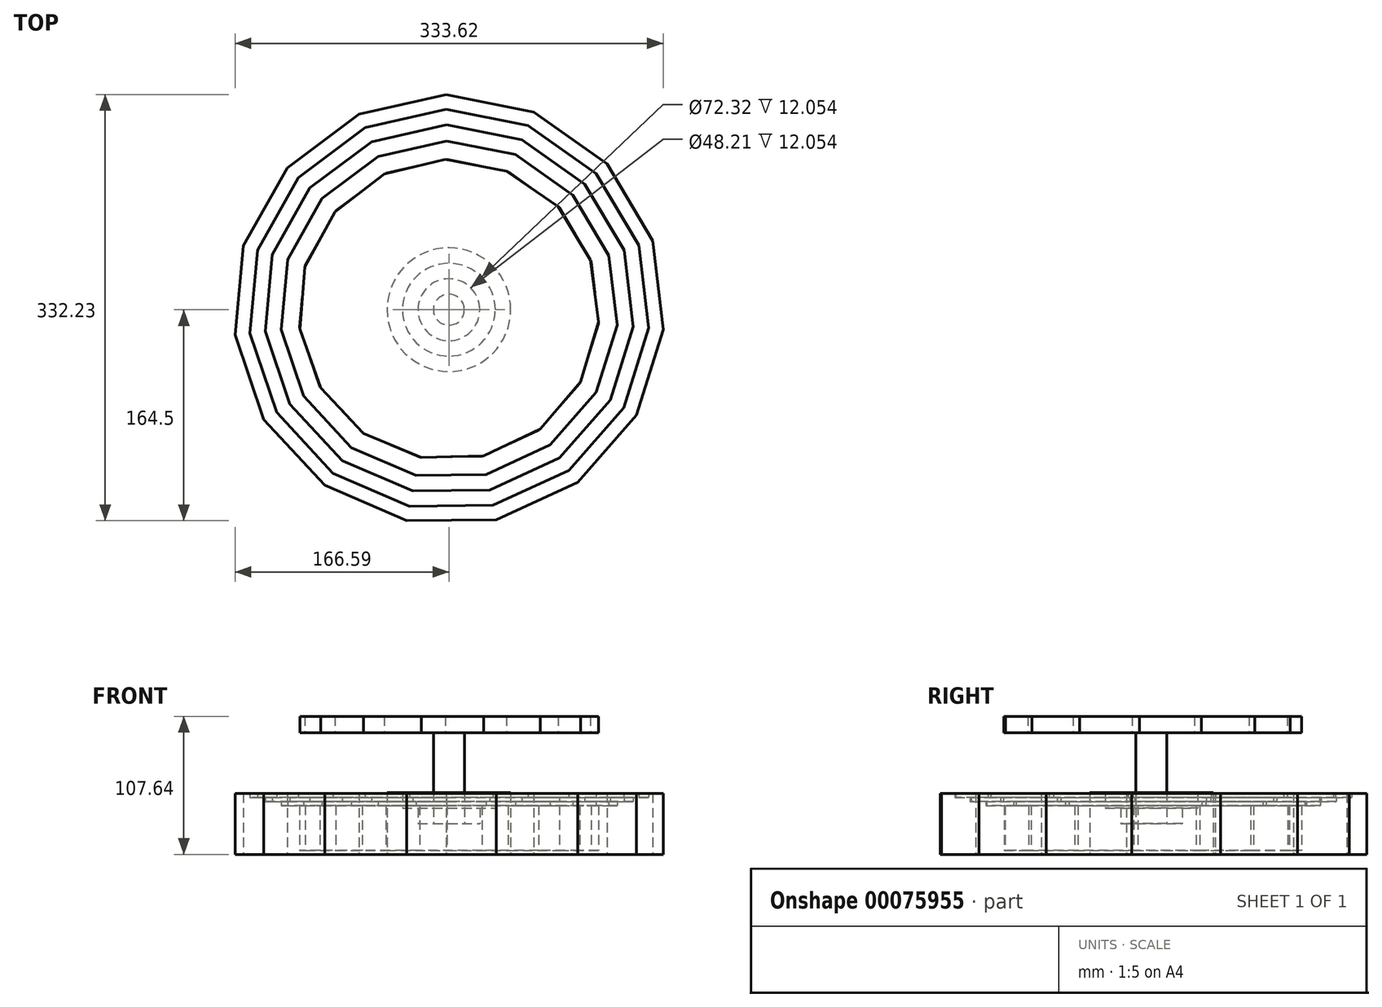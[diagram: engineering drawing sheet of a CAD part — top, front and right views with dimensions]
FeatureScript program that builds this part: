
annotation { "Feature Type Name" : "Feature", "Feature Type Description" : "" }
export const myFeature = defineFeature(function(context is Context, id is Id, definition is map)
    precondition{}
    {
        {
            var Q0;
            Q0=qCreatedBy(makeId("Top.planeOp"),FACE);
            var sketch = newSketch(context, id + "F0", { "sketchPlane" : qUnion([Q0])});
            skCircle(sketch, "E0.cCircle", {"center": v(0, 0) * mm, "radius": 164.07 * mm, "construction": true});
            skLineSegment(sketch, "E0.0", {"start": v(-160.17, 49.81) * mm, "end": v(-126.07, 110.65) * mm});
            skLineSegment(sketch, "E0.1", {"start": v(-126.07, 110.65) * mm, "end": v(-70.16, 152.36) * mm});
            skLineSegment(sketch, "E0.2", {"start": v(-70.16, 152.36) * mm, "end": v(-2.12, 167.73) * mm});
            skLineSegment(sketch, "E0.3", {"start": v(-2.12, 167.73) * mm, "end": v(66.28, 154.09) * mm});
            skLineSegment(sketch, "E0.4", {"start": v(66.28, 154.09) * mm, "end": v(123.22, 113.8) * mm});
            skLineSegment(sketch, "E0.5", {"start": v(123.22, 113.8) * mm, "end": v(158.86, 53.85) * mm});
            skLineSegment(sketch, "E0.6", {"start": v(158.86, 53.85) * mm, "end": v(167.03, -15.42) * mm});
            skLineSegment(sketch, "E0.7", {"start": v(167.03, -15.42) * mm, "end": v(146.32, -82.02) * mm});
            skLineSegment(sketch, "E0.8", {"start": v(146.32, -82.02) * mm, "end": v(100.3, -134.45) * mm});
            skLineSegment(sketch, "E0.9", {"start": v(100.3, -134.45) * mm, "end": v(36.95, -163.62) * mm});
            skLineSegment(sketch, "E0.10", {"start": v(36.95, -163.62) * mm, "end": v(-32.8, -164.5) * mm});
            skLineSegment(sketch, "E0.11", {"start": v(-32.8, -164.5) * mm, "end": v(-96.87, -136.94) * mm});
            skLineSegment(sketch, "E0.12", {"start": v(-96.87, -136.94) * mm, "end": v(-144.2, -85.7) * mm});
            skLineSegment(sketch, "E0.13", {"start": v(-144.2, -85.7) * mm, "end": v(-166.59, -19.64) * mm});
            skLineSegment(sketch, "E0.14", {"start": v(-166.59, -19.64) * mm, "end": v(-160.17, 49.81) * mm});
            skPoint(sketch, "E0.0.midPoint", {"position": v(-143.12, 80.23) * mm});
            skCircle(sketch, "E1.cCircle", {"center": v(0, 0) * mm, "radius": 152.82 * mm, "construction": true});
            skLineSegment(sketch, "E1.0", {"start": v(-149.18, 46.4) * mm, "end": v(-117.42, 103.06) * mm});
            skLineSegment(sketch, "E1.1", {"start": v(-117.42, 103.06) * mm, "end": v(-65.35, 141.9) * mm});
            skLineSegment(sketch, "E1.2", {"start": v(-65.35, 141.9) * mm, "end": v(-1.98, 156.22) * mm});
            skLineSegment(sketch, "E1.3", {"start": v(-1.98, 156.22) * mm, "end": v(61.73, 143.52) * mm});
            skLineSegment(sketch, "E1.4", {"start": v(61.73, 143.52) * mm, "end": v(114.77, 106) * mm});
            skLineSegment(sketch, "E1.5", {"start": v(114.77, 106) * mm, "end": v(147.96, 50.15) * mm});
            skLineSegment(sketch, "E1.6", {"start": v(147.96, 50.15) * mm, "end": v(155.57, -14.36) * mm});
            skLineSegment(sketch, "E1.7", {"start": v(155.57, -14.36) * mm, "end": v(136.28, -76.4) * mm});
            skLineSegment(sketch, "E1.8", {"start": v(136.28, -76.4) * mm, "end": v(93.42, -125.22) * mm});
            skLineSegment(sketch, "E1.9", {"start": v(93.42, -125.22) * mm, "end": v(34.41, -152.4) * mm});
            skLineSegment(sketch, "E1.10", {"start": v(34.41, -152.4) * mm, "end": v(-30.55, -153.21) * mm});
            skLineSegment(sketch, "E1.11", {"start": v(-30.55, -153.21) * mm, "end": v(-90.22, -127.54) * mm});
            skLineSegment(sketch, "E1.12", {"start": v(-90.22, -127.54) * mm, "end": v(-134.3, -79.82) * mm});
            skLineSegment(sketch, "E1.13", {"start": v(-134.3, -79.82) * mm, "end": v(-155.15, -18.3) * mm});
            skLineSegment(sketch, "E1.14", {"start": v(-155.15, -18.3) * mm, "end": v(-149.18, 46.4) * mm});
            skPoint(sketch, "E1.0.midPoint", {"position": v(-133.3, 74.73) * mm});
            skCircle(sketch, "E2.cCircle", {"center": v(0, 0) * mm, "radius": 140.97 * mm, "construction": true});
            skLineSegment(sketch, "E2.0", {"start": v(-137.62, 42.8) * mm, "end": v(-108.32, 95.07) * mm});
            skLineSegment(sketch, "E2.1", {"start": v(-108.32, 95.07) * mm, "end": v(-60.28, 130.91) * mm});
            skLineSegment(sketch, "E2.2", {"start": v(-60.28, 130.91) * mm, "end": v(-1.82, 144.11) * mm});
            skLineSegment(sketch, "E2.3", {"start": v(-1.82, 144.11) * mm, "end": v(56.95, 132.4) * mm});
            skLineSegment(sketch, "E2.4", {"start": v(56.95, 132.4) * mm, "end": v(105.88, 97.79) * mm});
            skLineSegment(sketch, "E2.5", {"start": v(105.88, 97.79) * mm, "end": v(136.5, 46.27) * mm});
            skLineSegment(sketch, "E2.6", {"start": v(136.5, 46.27) * mm, "end": v(143.51, -13.25) * mm});
            skLineSegment(sketch, "E2.7", {"start": v(143.51, -13.25) * mm, "end": v(125.72, -70.48) * mm});
            skLineSegment(sketch, "E2.8", {"start": v(125.72, -70.48) * mm, "end": v(86.18, -115.52) * mm});
            skLineSegment(sketch, "E2.9", {"start": v(86.18, -115.52) * mm, "end": v(31.75, -140.58) * mm});
            skLineSegment(sketch, "E2.10", {"start": v(31.75, -140.58) * mm, "end": v(-28.18, -141.34) * mm});
            skLineSegment(sketch, "E2.11", {"start": v(-28.18, -141.34) * mm, "end": v(-83.23, -117.66) * mm});
            skLineSegment(sketch, "E2.12", {"start": v(-83.23, -117.66) * mm, "end": v(-123.9, -73.64) * mm});
            skLineSegment(sketch, "E2.13", {"start": v(-123.9, -73.64) * mm, "end": v(-143.13, -16.88) * mm});
            skLineSegment(sketch, "E2.14", {"start": v(-143.13, -16.88) * mm, "end": v(-137.62, 42.8) * mm});
            skPoint(sketch, "E2.0.midPoint", {"position": v(-122.97, 68.94) * mm});
            skCircle(sketch, "E3.cCircle", {"center": v(0, 0) * mm, "radius": 128.76 * mm, "construction": true});
            skLineSegment(sketch, "E3.0", {"start": v(-125.7, 39.1) * mm, "end": v(-98.94, 86.84) * mm});
            skLineSegment(sketch, "E3.1", {"start": v(-98.94, 86.84) * mm, "end": v(-55.06, 119.57) * mm});
            skLineSegment(sketch, "E3.2", {"start": v(-55.06, 119.57) * mm, "end": v(-1.67, 131.63) * mm});
            skLineSegment(sketch, "E3.3", {"start": v(-1.67, 131.63) * mm, "end": v(52.02, 120.93) * mm});
            skLineSegment(sketch, "E3.4", {"start": v(52.02, 120.93) * mm, "end": v(96.7, 89.32) * mm});
            skLineSegment(sketch, "E3.5", {"start": v(96.7, 89.32) * mm, "end": v(124.67, 42.26) * mm});
            skLineSegment(sketch, "E3.6", {"start": v(124.67, 42.26) * mm, "end": v(131.08, -12.1) * mm});
            skLineSegment(sketch, "E3.7", {"start": v(131.08, -12.1) * mm, "end": v(114.83, -64.37) * mm});
            skLineSegment(sketch, "E3.8", {"start": v(114.83, -64.37) * mm, "end": v(78.72, -105.51) * mm});
            skLineSegment(sketch, "E3.9", {"start": v(78.72, -105.51) * mm, "end": v(29, -128.4) * mm});
            skLineSegment(sketch, "E3.10", {"start": v(29, -128.4) * mm, "end": v(-25.74, -129.1) * mm});
            skLineSegment(sketch, "E3.11", {"start": v(-25.74, -129.1) * mm, "end": v(-76.02, -107.47) * mm});
            skLineSegment(sketch, "E3.12", {"start": v(-76.02, -107.47) * mm, "end": v(-113.16, -67.26) * mm});
            skLineSegment(sketch, "E3.13", {"start": v(-113.16, -67.26) * mm, "end": v(-130.74, -15.42) * mm});
            skLineSegment(sketch, "E3.14", {"start": v(-130.74, -15.42) * mm, "end": v(-125.7, 39.1) * mm});
            skPoint(sketch, "E3.0.midPoint", {"position": v(-112.32, 62.97) * mm});
            skCircle(sketch, "E4.cCircle", {"center": v(0, 0) * mm, "radius": 114.54 * mm, "construction": true});
            skLineSegment(sketch, "E4.0", {"start": v(-111.81, 34.77) * mm, "end": v(-88, 77.24) * mm});
            skLineSegment(sketch, "E4.1", {"start": v(-88, 77.24) * mm, "end": v(-48.98, 106.36) * mm});
            skLineSegment(sketch, "E4.2", {"start": v(-48.98, 106.36) * mm, "end": v(-1.48, 117.08) * mm});
            skLineSegment(sketch, "E4.3", {"start": v(-1.48, 117.08) * mm, "end": v(46.27, 107.57) * mm});
            skLineSegment(sketch, "E4.4", {"start": v(46.27, 107.57) * mm, "end": v(86.02, 79.45) * mm});
            skLineSegment(sketch, "E4.5", {"start": v(86.02, 79.45) * mm, "end": v(110.9, 37.6) * mm});
            skLineSegment(sketch, "E4.6", {"start": v(110.9, 37.6) * mm, "end": v(116.6, -10.76) * mm});
            skLineSegment(sketch, "E4.7", {"start": v(116.6, -10.76) * mm, "end": v(102.14, -57.26) * mm});
            skLineSegment(sketch, "E4.8", {"start": v(102.14, -57.26) * mm, "end": v(70.02, -93.85) * mm});
            skLineSegment(sketch, "E4.9", {"start": v(70.02, -93.85) * mm, "end": v(25.8, -114.22) * mm});
            skLineSegment(sketch, "E4.10", {"start": v(25.8, -114.22) * mm, "end": v(-22.9, -114.83) * mm});
            skLineSegment(sketch, "E4.11", {"start": v(-22.9, -114.83) * mm, "end": v(-67.62, -95.6) * mm});
            skLineSegment(sketch, "E4.12", {"start": v(-67.62, -95.6) * mm, "end": v(-100.66, -59.83) * mm});
            skLineSegment(sketch, "E4.13", {"start": v(-100.66, -59.83) * mm, "end": v(-116.29, -13.71) * mm});
            skLineSegment(sketch, "E4.14", {"start": v(-116.29, -13.71) * mm, "end": v(-111.81, 34.77) * mm});
            skPoint(sketch, "E4.0.midPoint", {"position": v(-99.9, 56) * mm});
            skCircle(sketch, "E5.cCircle", {"center": v(0, 0) * mm, "radius": 101.53 * mm, "construction": true});
            skLineSegment(sketch, "E5.0", {"start": v(-99.12, 30.82) * mm, "end": v(-78, 68.47) * mm});
            skLineSegment(sketch, "E5.1", {"start": v(-78, 68.47) * mm, "end": v(-43.42, 94.28) * mm});
            skLineSegment(sketch, "E5.2", {"start": v(-43.42, 94.28) * mm, "end": v(-1.31, 103.79) * mm});
            skLineSegment(sketch, "E5.3", {"start": v(-1.31, 103.79) * mm, "end": v(41.01, 95.35) * mm});
            skLineSegment(sketch, "E5.4", {"start": v(41.01, 95.35) * mm, "end": v(76.25, 70.43) * mm});
            skLineSegment(sketch, "E5.5", {"start": v(76.25, 70.43) * mm, "end": v(98.3, 33.32) * mm});
            skLineSegment(sketch, "E5.6", {"start": v(98.3, 33.32) * mm, "end": v(103.36, -9.54) * mm});
            skLineSegment(sketch, "E5.7", {"start": v(103.36, -9.54) * mm, "end": v(90.54, -50.76) * mm});
            skLineSegment(sketch, "E5.8", {"start": v(90.54, -50.76) * mm, "end": v(62.07, -83.2) * mm});
            skLineSegment(sketch, "E5.9", {"start": v(62.07, -83.2) * mm, "end": v(22.86, -101.25) * mm});
            skLineSegment(sketch, "E5.10", {"start": v(22.86, -101.25) * mm, "end": v(-20.3, -101.8) * mm});
            skLineSegment(sketch, "E5.11", {"start": v(-20.3, -101.8) * mm, "end": v(-59.94, -84.74) * mm});
            skLineSegment(sketch, "E5.12", {"start": v(-59.94, -84.74) * mm, "end": v(-89.23, -53.03) * mm});
            skLineSegment(sketch, "E5.13", {"start": v(-89.23, -53.03) * mm, "end": v(-103.08, -12.16) * mm});
            skLineSegment(sketch, "E5.14", {"start": v(-103.08, -12.16) * mm, "end": v(-99.12, 30.82) * mm});
            skPoint(sketch, "E5.0.midPoint", {"position": v(-88.56, 49.65) * mm});
            skCircle(sketch, "E6.cCircle", {"center": v(0, 0) * mm, "radius": 89.42 * mm, "construction": true});
            skLineSegment(sketch, "E6.0", {"start": v(-87.3, 27.15) * mm, "end": v(-68.7, 60.3) * mm});
            skLineSegment(sketch, "E6.1", {"start": v(-68.7, 60.3) * mm, "end": v(-38.24, 83.03) * mm});
            skLineSegment(sketch, "E6.2", {"start": v(-38.24, 83.03) * mm, "end": v(-1.16, 91.4) * mm});
            skLineSegment(sketch, "E6.3", {"start": v(-1.16, 91.4) * mm, "end": v(36.12, 83.97) * mm});
            skLineSegment(sketch, "E6.4", {"start": v(36.12, 83.97) * mm, "end": v(67.15, 62.02) * mm});
            skLineSegment(sketch, "E6.5", {"start": v(67.15, 62.02) * mm, "end": v(86.58, 29.35) * mm});
            skLineSegment(sketch, "E6.6", {"start": v(86.58, 29.35) * mm, "end": v(91.03, -8.4) * mm});
            skLineSegment(sketch, "E6.7", {"start": v(91.03, -8.4) * mm, "end": v(79.74, -44.7) * mm});
            skLineSegment(sketch, "E6.8", {"start": v(79.74, -44.7) * mm, "end": v(54.66, -73.27) * mm});
            skLineSegment(sketch, "E6.9", {"start": v(54.66, -73.27) * mm, "end": v(20.14, -89.17) * mm});
            skLineSegment(sketch, "E6.10", {"start": v(20.14, -89.17) * mm, "end": v(-17.87, -89.65) * mm});
            skLineSegment(sketch, "E6.11", {"start": v(-17.87, -89.65) * mm, "end": v(-52.8, -74.63) * mm});
            skLineSegment(sketch, "E6.12", {"start": v(-52.8, -74.63) * mm, "end": v(-78.58, -46.7) * mm});
            skLineSegment(sketch, "E6.13", {"start": v(-78.58, -46.7) * mm, "end": v(-90.79, -10.7) * mm});
            skLineSegment(sketch, "E6.14", {"start": v(-90.79, -10.7) * mm, "end": v(-87.3, 27.15) * mm});
            skPoint(sketch, "E6.0.midPoint", {"position": v(-78, 43.72) * mm});
            skCircle(sketch, "E7.cCircle", {"center": v(0, 0) * mm, "radius": 79.7 * mm, "construction": true});
            skLineSegment(sketch, "E7.0", {"start": v(-77.8, 24.2) * mm, "end": v(-61.23, 53.74) * mm});
            skLineSegment(sketch, "E7.1", {"start": v(-61.23, 53.74) * mm, "end": v(-34.08, 74) * mm});
            skLineSegment(sketch, "E7.2", {"start": v(-34.08, 74) * mm, "end": v(-1.03, 81.47) * mm});
            skLineSegment(sketch, "E7.3", {"start": v(-1.03, 81.47) * mm, "end": v(32.2, 74.84) * mm});
            skLineSegment(sketch, "E7.4", {"start": v(32.2, 74.84) * mm, "end": v(59.85, 55.28) * mm});
            skLineSegment(sketch, "E7.5", {"start": v(59.85, 55.28) * mm, "end": v(77.16, 26.15) * mm});
            skLineSegment(sketch, "E7.6", {"start": v(77.16, 26.15) * mm, "end": v(81.13, -7.49) * mm});
            skLineSegment(sketch, "E7.7", {"start": v(81.13, -7.49) * mm, "end": v(71.07, -39.84) * mm});
            skLineSegment(sketch, "E7.8", {"start": v(71.07, -39.84) * mm, "end": v(48.72, -65.3) * mm});
            skLineSegment(sketch, "E7.9", {"start": v(48.72, -65.3) * mm, "end": v(17.95, -79.47) * mm});
            skLineSegment(sketch, "E7.10", {"start": v(17.95, -79.47) * mm, "end": v(-15.93, -79.9) * mm});
            skLineSegment(sketch, "E7.11", {"start": v(-15.93, -79.9) * mm, "end": v(-47.05, -66.51) * mm});
            skLineSegment(sketch, "E7.12", {"start": v(-47.05, -66.51) * mm, "end": v(-70.04, -41.63) * mm});
            skLineSegment(sketch, "E7.13", {"start": v(-70.04, -41.63) * mm, "end": v(-80.91, -9.54) * mm});
            skLineSegment(sketch, "E7.14", {"start": v(-80.91, -9.54) * mm, "end": v(-77.8, 24.2) * mm});
            skPoint(sketch, "E7.0.midPoint", {"position": v(-69.51, 38.97) * mm});
            skCircle(sketch, "E8.cCircle", {"center": v(0, 0) * mm, "radius": 67.2 * mm, "construction": true});
            skLineSegment(sketch, "E8.0", {"start": v(-65.61, 20.4) * mm, "end": v(-51.64, 45.33) * mm});
            skLineSegment(sketch, "E8.1", {"start": v(-51.64, 45.33) * mm, "end": v(-28.74, 62.41) * mm});
            skLineSegment(sketch, "E8.2", {"start": v(-28.74, 62.41) * mm, "end": v(-0.87, 68.7) * mm});
            skLineSegment(sketch, "E8.3", {"start": v(-0.87, 68.7) * mm, "end": v(27.15, 63.12) * mm});
            skLineSegment(sketch, "E8.4", {"start": v(27.15, 63.12) * mm, "end": v(50.48, 46.62) * mm});
            skLineSegment(sketch, "E8.5", {"start": v(50.48, 46.62) * mm, "end": v(65.07, 22.06) * mm});
            skLineSegment(sketch, "E8.6", {"start": v(65.07, 22.06) * mm, "end": v(68.42, -6.32) * mm});
            skLineSegment(sketch, "E8.7", {"start": v(68.42, -6.32) * mm, "end": v(59.94, -33.6) * mm});
            skLineSegment(sketch, "E8.8", {"start": v(59.94, -33.6) * mm, "end": v(41.09, -55.07) * mm});
            skLineSegment(sketch, "E8.9", {"start": v(41.09, -55.07) * mm, "end": v(15.14, -67.02) * mm});
            skLineSegment(sketch, "E8.10", {"start": v(15.14, -67.02) * mm, "end": v(-13.43, -67.38) * mm});
            skLineSegment(sketch, "E8.11", {"start": v(-13.43, -67.38) * mm, "end": v(-39.68, -56.1) * mm});
            skLineSegment(sketch, "E8.12", {"start": v(-39.68, -56.1) * mm, "end": v(-59.07, -35.1) * mm});
            skLineSegment(sketch, "E8.13", {"start": v(-59.07, -35.1) * mm, "end": v(-68.24, -8.05) * mm});
            skLineSegment(sketch, "E8.14", {"start": v(-68.24, -8.05) * mm, "end": v(-65.61, 20.4) * mm});
            skPoint(sketch, "E8.0.midPoint", {"position": v(-58.63, 32.87) * mm});
            skCircle(sketch, "E9.cCircle", {"center": v(0, 0) * mm, "radius": 54.94 * mm, "construction": true});
            skLineSegment(sketch, "E9.0", {"start": v(-53.63, 16.68) * mm, "end": v(-42.21, 37.05) * mm});
            skLineSegment(sketch, "E9.1", {"start": v(-42.21, 37.05) * mm, "end": v(-23.5, 51.02) * mm});
            skLineSegment(sketch, "E9.2", {"start": v(-23.5, 51.02) * mm, "end": v(-0.71, 56.16) * mm});
            skLineSegment(sketch, "E9.3", {"start": v(-0.71, 56.16) * mm, "end": v(22.2, 51.6) * mm});
            skLineSegment(sketch, "E9.4", {"start": v(22.2, 51.6) * mm, "end": v(41.26, 38.1) * mm});
            skLineSegment(sketch, "E9.5", {"start": v(41.26, 38.1) * mm, "end": v(53.2, 18.03) * mm});
            skLineSegment(sketch, "E9.6", {"start": v(53.2, 18.03) * mm, "end": v(55.93, -5.16) * mm});
            skLineSegment(sketch, "E9.7", {"start": v(55.93, -5.16) * mm, "end": v(49, -27.47) * mm});
            skLineSegment(sketch, "E9.8", {"start": v(49, -27.47) * mm, "end": v(33.59, -45.02) * mm});
            skLineSegment(sketch, "E9.9", {"start": v(33.59, -45.02) * mm, "end": v(12.37, -54.79) * mm});
            skLineSegment(sketch, "E9.10", {"start": v(12.37, -54.79) * mm, "end": v(-10.98, -55.08) * mm});
            skLineSegment(sketch, "E9.11", {"start": v(-10.98, -55.08) * mm, "end": v(-32.44, -45.86) * mm});
            skLineSegment(sketch, "E9.12", {"start": v(-32.44, -45.86) * mm, "end": v(-48.28, -28.7) * mm});
            skLineSegment(sketch, "E9.13", {"start": v(-48.28, -28.7) * mm, "end": v(-55.78, -6.58) * mm});
            skLineSegment(sketch, "E9.14", {"start": v(-55.78, -6.58) * mm, "end": v(-53.63, 16.68) * mm});
            skPoint(sketch, "E9.0.midPoint", {"position": v(-47.92, 26.87) * mm});
            skCircle(sketch, "E10.cCircle", {"center": v(0, 0) * mm, "radius": 44.85 * mm, "construction": true});
            skLineSegment(sketch, "E10.0", {"start": v(-43.78, 13.62) * mm, "end": v(-34.46, 30.25) * mm});
            skLineSegment(sketch, "E10.1", {"start": v(-34.46, 30.25) * mm, "end": v(-19.18, 41.65) * mm});
            skLineSegment(sketch, "E10.2", {"start": v(-19.18, 41.65) * mm, "end": v(-0.58, 45.85) * mm});
            skLineSegment(sketch, "E10.3", {"start": v(-0.58, 45.85) * mm, "end": v(18.12, 42.12) * mm});
            skLineSegment(sketch, "E10.4", {"start": v(18.12, 42.12) * mm, "end": v(33.68, 31.1) * mm});
            skLineSegment(sketch, "E10.5", {"start": v(33.68, 31.1) * mm, "end": v(43.42, 14.72) * mm});
            skLineSegment(sketch, "E10.6", {"start": v(43.42, 14.72) * mm, "end": v(45.65, -4.21) * mm});
            skLineSegment(sketch, "E10.7", {"start": v(45.65, -4.21) * mm, "end": v(40, -22.42) * mm});
            skLineSegment(sketch, "E10.8", {"start": v(40, -22.42) * mm, "end": v(27.42, -36.75) * mm});
            skLineSegment(sketch, "E10.9", {"start": v(27.42, -36.75) * mm, "end": v(10.1, -44.72) * mm});
            skLineSegment(sketch, "E10.10", {"start": v(10.1, -44.72) * mm, "end": v(-8.96, -44.96) * mm});
            skLineSegment(sketch, "E10.11", {"start": v(-8.96, -44.96) * mm, "end": v(-26.48, -37.43) * mm});
            skLineSegment(sketch, "E10.12", {"start": v(-26.48, -37.43) * mm, "end": v(-39.41, -23.43) * mm});
            skLineSegment(sketch, "E10.13", {"start": v(-39.41, -23.43) * mm, "end": v(-45.53, -5.37) * mm});
            skLineSegment(sketch, "E10.14", {"start": v(-45.53, -5.37) * mm, "end": v(-43.78, 13.62) * mm});
            skPoint(sketch, "E10.0.midPoint", {"position": v(-39.12, 21.93) * mm});
            skCircle(sketch, "E11.cCircle", {"center": v(0, 0) * mm, "radius": 34.6 * mm, "construction": true});
            skLineSegment(sketch, "E11.0", {"start": v(-33.78, 10.5) * mm, "end": v(-26.58, 23.33) * mm});
            skLineSegment(sketch, "E11.1", {"start": v(-26.58, 23.33) * mm, "end": v(-14.8, 32.13) * mm});
            skLineSegment(sketch, "E11.2", {"start": v(-14.8, 32.13) * mm, "end": v(-0.45, 35.37) * mm});
            skLineSegment(sketch, "E11.3", {"start": v(-0.45, 35.37) * mm, "end": v(13.98, 32.5) * mm});
            skLineSegment(sketch, "E11.4", {"start": v(13.98, 32.5) * mm, "end": v(25.98, 24) * mm});
            skLineSegment(sketch, "E11.5", {"start": v(25.98, 24) * mm, "end": v(33.5, 11.36) * mm});
            skLineSegment(sketch, "E11.6", {"start": v(33.5, 11.36) * mm, "end": v(35.22, -3.25) * mm});
            skLineSegment(sketch, "E11.7", {"start": v(35.22, -3.25) * mm, "end": v(30.85, -17.3) * mm});
            skLineSegment(sketch, "E11.8", {"start": v(30.85, -17.3) * mm, "end": v(21.15, -28.35) * mm});
            skLineSegment(sketch, "E11.9", {"start": v(21.15, -28.35) * mm, "end": v(7.8, -34.5) * mm});
            skLineSegment(sketch, "E11.10", {"start": v(7.8, -34.5) * mm, "end": v(-6.92, -34.69) * mm});
            skLineSegment(sketch, "E11.11", {"start": v(-6.92, -34.69) * mm, "end": v(-20.43, -28.88) * mm});
            skLineSegment(sketch, "E11.12", {"start": v(-20.43, -28.88) * mm, "end": v(-30.4, -18.07) * mm});
            skLineSegment(sketch, "E11.13", {"start": v(-30.4, -18.07) * mm, "end": v(-35.13, -4.14) * mm});
            skLineSegment(sketch, "E11.14", {"start": v(-35.13, -4.14) * mm, "end": v(-33.78, 10.5) * mm});
            skPoint(sketch, "E11.0.midPoint", {"position": v(-30.18, 16.92) * mm});
            skCircle(sketch, "E12.cCircle", {"center": v(0, 0) * mm, "radius": 25.78 * mm, "construction": true});
            skLineSegment(sketch, "E12.0", {"start": v(-25.17, 7.83) * mm, "end": v(-19.81, 17.39) * mm});
            skLineSegment(sketch, "E12.1", {"start": v(-19.81, 17.39) * mm, "end": v(-11.03, 23.94) * mm});
            skLineSegment(sketch, "E12.2", {"start": v(-11.03, 23.94) * mm, "end": v(-0.33, 26.36) * mm});
            skLineSegment(sketch, "E12.3", {"start": v(-0.33, 26.36) * mm, "end": v(10.42, 24.22) * mm});
            skLineSegment(sketch, "E12.4", {"start": v(10.42, 24.22) * mm, "end": v(19.36, 17.89) * mm});
            skLineSegment(sketch, "E12.5", {"start": v(19.36, 17.89) * mm, "end": v(24.97, 8.46) * mm});
            skLineSegment(sketch, "E12.6", {"start": v(24.97, 8.46) * mm, "end": v(26.25, -2.42) * mm});
            skLineSegment(sketch, "E12.7", {"start": v(26.25, -2.42) * mm, "end": v(23, -12.9) * mm});
            skLineSegment(sketch, "E12.8", {"start": v(23, -12.9) * mm, "end": v(15.76, -21.13) * mm});
            skLineSegment(sketch, "E12.9", {"start": v(15.76, -21.13) * mm, "end": v(5.8, -25.71) * mm});
            skLineSegment(sketch, "E12.10", {"start": v(5.8, -25.71) * mm, "end": v(-5.15, -25.85) * mm});
            skLineSegment(sketch, "E12.11", {"start": v(-5.15, -25.85) * mm, "end": v(-15.22, -21.52) * mm});
            skLineSegment(sketch, "E12.12", {"start": v(-15.22, -21.52) * mm, "end": v(-22.66, -13.47) * mm});
            skLineSegment(sketch, "E12.13", {"start": v(-22.66, -13.47) * mm, "end": v(-26.18, -3.09) * mm});
            skLineSegment(sketch, "E12.14", {"start": v(-26.18, -3.09) * mm, "end": v(-25.17, 7.83) * mm});
            skPoint(sketch, "E12.0.midPoint", {"position": v(-22.5, 12.6) * mm});
            skCircle(sketch, "E13.cCircle", {"center": v(0, 0) * mm, "radius": 18.22 * mm, "construction": true});
            skLineSegment(sketch, "E13.0", {"start": v(-17.78, 5.53) * mm, "end": v(-14, 12.29) * mm});
            skLineSegment(sketch, "E13.1", {"start": v(-14, 12.29) * mm, "end": v(-7.79, 16.92) * mm});
            skLineSegment(sketch, "E13.2", {"start": v(-7.79, 16.92) * mm, "end": v(-0.24, 18.62) * mm});
            skLineSegment(sketch, "E13.3", {"start": v(-0.24, 18.62) * mm, "end": v(7.36, 17.1) * mm});
            skLineSegment(sketch, "E13.4", {"start": v(7.36, 17.1) * mm, "end": v(13.68, 12.64) * mm});
            skLineSegment(sketch, "E13.5", {"start": v(13.68, 12.64) * mm, "end": v(17.64, 5.98) * mm});
            skLineSegment(sketch, "E13.6", {"start": v(17.64, 5.98) * mm, "end": v(18.54, -1.71) * mm});
            skLineSegment(sketch, "E13.7", {"start": v(18.54, -1.71) * mm, "end": v(16.24, -9.1) * mm});
            skLineSegment(sketch, "E13.8", {"start": v(16.24, -9.1) * mm, "end": v(11.14, -14.93) * mm});
            skLineSegment(sketch, "E13.9", {"start": v(11.14, -14.93) * mm, "end": v(4.1, -18.17) * mm});
            skLineSegment(sketch, "E13.10", {"start": v(4.1, -18.17) * mm, "end": v(-3.64, -18.26) * mm});
            skLineSegment(sketch, "E13.11", {"start": v(-3.64, -18.26) * mm, "end": v(-10.75, -15.2) * mm});
            skLineSegment(sketch, "E13.12", {"start": v(-10.75, -15.2) * mm, "end": v(-16, -9.51) * mm});
            skLineSegment(sketch, "E13.13", {"start": v(-16, -9.51) * mm, "end": v(-18.5, -2.18) * mm});
            skLineSegment(sketch, "E13.14", {"start": v(-18.5, -2.18) * mm, "end": v(-17.78, 5.53) * mm});
            skPoint(sketch, "E13.0.midPoint", {"position": v(-15.89, 8.9) * mm});
            skCircle(sketch, "E14.cCircle", {"center": v(0, 0) * mm, "radius": 12.35 * mm, "construction": true});
            skLineSegment(sketch, "E14.0", {"start": v(-12.06, 3.75) * mm, "end": v(-9.5, 8.33) * mm});
            skLineSegment(sketch, "E14.1", {"start": v(-9.5, 8.33) * mm, "end": v(-5.28, 11.47) * mm});
            skLineSegment(sketch, "E14.2", {"start": v(-5.28, 11.47) * mm, "end": v(-0.16, 12.63) * mm});
            skLineSegment(sketch, "E14.3", {"start": v(-0.16, 12.63) * mm, "end": v(4.99, 11.6) * mm});
            skLineSegment(sketch, "E14.4", {"start": v(4.99, 11.6) * mm, "end": v(9.28, 8.57) * mm});
            skLineSegment(sketch, "E14.5", {"start": v(9.28, 8.57) * mm, "end": v(11.96, 4.05) * mm});
            skLineSegment(sketch, "E14.6", {"start": v(11.96, 4.05) * mm, "end": v(12.57, -1.16) * mm});
            skLineSegment(sketch, "E14.7", {"start": v(12.57, -1.16) * mm, "end": v(11.02, -6.18) * mm});
            skLineSegment(sketch, "E14.8", {"start": v(11.02, -6.18) * mm, "end": v(7.55, -10.12) * mm});
            skLineSegment(sketch, "E14.9", {"start": v(7.55, -10.12) * mm, "end": v(2.78, -12.32) * mm});
            skLineSegment(sketch, "E14.10", {"start": v(2.78, -12.32) * mm, "end": v(-2.47, -12.38) * mm});
            skLineSegment(sketch, "E14.11", {"start": v(-2.47, -12.38) * mm, "end": v(-7.3, -10.3) * mm});
            skLineSegment(sketch, "E14.12", {"start": v(-7.3, -10.3) * mm, "end": v(-10.86, -6.45) * mm});
            skLineSegment(sketch, "E14.13", {"start": v(-10.86, -6.45) * mm, "end": v(-12.54, -1.48) * mm});
            skLineSegment(sketch, "E14.14", {"start": v(-12.54, -1.48) * mm, "end": v(-12.06, 3.75) * mm});
            skPoint(sketch, "E14.0.midPoint", {"position": v(-10.77, 6.04) * mm});
            skCircle(sketch, "E15.cCircle", {"center": v(0, 0) * mm, "radius": 7.79 * mm, "construction": true});
            skLineSegment(sketch, "E15.0", {"start": v(-7.6, 2.36) * mm, "end": v(-5.98, 5.25) * mm});
            skLineSegment(sketch, "E15.1", {"start": v(-5.98, 5.25) * mm, "end": v(-3.33, 7.23) * mm});
            skLineSegment(sketch, "E15.2", {"start": v(-3.33, 7.23) * mm, "end": v(-0.1, 7.96) * mm});
            skLineSegment(sketch, "E15.3", {"start": v(-0.1, 7.96) * mm, "end": v(3.15, 7.31) * mm});
            skLineSegment(sketch, "E15.4", {"start": v(3.15, 7.31) * mm, "end": v(5.85, 5.4) * mm});
            skLineSegment(sketch, "E15.5", {"start": v(5.85, 5.4) * mm, "end": v(7.54, 2.56) * mm});
            skLineSegment(sketch, "E15.6", {"start": v(7.54, 2.56) * mm, "end": v(7.93, -0.73) * mm});
            skLineSegment(sketch, "E15.7", {"start": v(7.93, -0.73) * mm, "end": v(6.94, -3.9) * mm});
            skLineSegment(sketch, "E15.8", {"start": v(6.94, -3.9) * mm, "end": v(4.76, -6.38) * mm});
            skLineSegment(sketch, "E15.9", {"start": v(4.76, -6.38) * mm, "end": v(1.75, -7.77) * mm});
            skLineSegment(sketch, "E15.10", {"start": v(1.75, -7.77) * mm, "end": v(-1.56, -7.8) * mm});
            skLineSegment(sketch, "E15.11", {"start": v(-1.56, -7.8) * mm, "end": v(-4.6, -6.5) * mm});
            skLineSegment(sketch, "E15.12", {"start": v(-4.6, -6.5) * mm, "end": v(-6.84, -4.07) * mm});
            skLineSegment(sketch, "E15.13", {"start": v(-6.84, -4.07) * mm, "end": v(-7.9, -0.93) * mm});
            skLineSegment(sketch, "E15.14", {"start": v(-7.9, -0.93) * mm, "end": v(-7.6, 2.36) * mm});
            skPoint(sketch, "E15.0.midPoint", {"position": v(-6.8, 3.8) * mm});
            skSolve(sketch);
        }
        {
            var Q0;
            Q0=makeQuery(id+"F0.imprint","IMPRINT",FACE,{"disambiguationData":[TD([[makeQuery(id+"F0.imprint","IMPRINT",EDGE,{"derivedFrom":sQuery(id+"F0.wireOp",EDGE,"E14.0")}),-1.0]])]});
            var Q1;
            Q1=makeQuery(id+"F0.imprint","IMPRINT",FACE,{"disambiguationData":[TD([[makeQuery(id+"F0.imprint","IMPRINT",EDGE,{"derivedFrom":sQuery(id+"F0.wireOp",EDGE,"E15.0")}),-1.0]])]});
            extrude(context, id + "F1", {"entities" : qUnion([Q0, Q1]), "depth" : 3.17 * mm});
        }
        {
            var Q0;
            Q0=makeQuery(id+"F0.imprint","IMPRINT",FACE,{"disambiguationData":[TD([[makeQuery(id+"F0.imprint","IMPRINT",EDGE,{"derivedFrom":sQuery(id+"F0.wireOp",EDGE,"E13.0")}),-1.0]])]});
            var Q1;
            Q1=makeQuery(id+"F0.imprint","IMPRINT",FACE,{"disambiguationData":[TD([[makeQuery(id+"F0.imprint","IMPRINT",EDGE,{"derivedFrom":sQuery(id+"F0.wireOp",EDGE,"E12.0")}),-1.0]])]});
            var Q2;
            Q2=makeQuery(id+"F0.imprint","IMPRINT",FACE,{"disambiguationData":[TD([[makeQuery(id+"F0.imprint","IMPRINT",EDGE,{"derivedFrom":sQuery(id+"F0.wireOp",EDGE,"E11.0")}),-1.0]])]});
            var Q3;
            Q3=makeQuery(id+"F0.imprint","IMPRINT",FACE,{"disambiguationData":[TD([[makeQuery(id+"F0.imprint","IMPRINT",EDGE,{"derivedFrom":sQuery(id+"F0.wireOp",EDGE,"E10.0")}),-1.0]])]});
            var Q4;
            Q4=makeQuery(id+"F0.imprint","IMPRINT",FACE,{"disambiguationData":[TD([[makeQuery(id+"F0.imprint","IMPRINT",EDGE,{"derivedFrom":sQuery(id+"F0.wireOp",EDGE,"E9.0")}),-1.0]])]});
            var Q5;
            Q5=makeQuery(id+"F0.imprint","IMPRINT",FACE,{"disambiguationData":[TD([[makeQuery(id+"F0.imprint","IMPRINT",EDGE,{"derivedFrom":sQuery(id+"F0.wireOp",EDGE,"E8.0")}),-1.0]])]});
            var Q6;
            Q6=makeQuery(id+"F0.imprint","IMPRINT",FACE,{"disambiguationData":[TD([[makeQuery(id+"F0.imprint","IMPRINT",EDGE,{"derivedFrom":sQuery(id+"F0.wireOp",EDGE,"E7.0")}),-1.0]])]});
            var Q7;
            Q7=makeQuery(id+"F0.imprint","IMPRINT",FACE,{"disambiguationData":[TD([[makeQuery(id+"F0.imprint","IMPRINT",EDGE,{"derivedFrom":sQuery(id+"F0.wireOp",EDGE,"E6.0")}),-1.0]])]});
            var Q8;
            Q8=makeQuery(id+"F0.imprint","IMPRINT",FACE,{"disambiguationData":[TD([[makeQuery(id+"F0.imprint","IMPRINT",EDGE,{"derivedFrom":sQuery(id+"F0.wireOp",EDGE,"E5.0")}),-1.0]])]});
            var Q9;
            Q9=makeQuery(id+"F0.imprint","IMPRINT",FACE,{"disambiguationData":[TD([[makeQuery(id+"F0.imprint","IMPRINT",EDGE,{"derivedFrom":sQuery(id+"F0.wireOp",EDGE,"E4.0")}),-1.0]])]});
            extrude(context, id + "F2", {"entities" : qUnion([Q0, Q1, Q2, Q3, Q4, Q5, Q6, Q7, Q8, Q9]), "operationType" : NewBodyOperationType.ADD, "depth" : 3.17 * mm});
        }
        {
            var Q0;
            Q0=makeQuery(id+"F0.imprint","IMPRINT",FACE,{"disambiguationData":[TD([[makeQuery(id+"F0.imprint","IMPRINT",EDGE,{"derivedFrom":sQuery(id+"F0.wireOp",EDGE,"E3.0")}),-1.0]])]});
            extrude(context, id + "F3", {"entities" : qUnion([Q0]), "operationType" : NewBodyOperationType.ADD, "depth" : 38.1 * mm});
        }
        {
            var Q0;
            Q0=makeQuery(id+"F0.imprint","IMPRINT",FACE,{"disambiguationData":[TD([[makeQuery(id+"F0.imprint","IMPRINT",EDGE,{"derivedFrom":sQuery(id+"F0.wireOp",EDGE,"E2.0")}),-1.0]])]});
            extrude(context, id + "F4", {"entities" : qUnion([Q0]), "operationType" : NewBodyOperationType.ADD, "depth" : 41.27 * mm});
        }
        {
            var Q0;
            Q0=makeQuery(id+"F0.imprint","IMPRINT",FACE,{"disambiguationData":[TD([[makeQuery(id+"F0.imprint","IMPRINT",EDGE,{"derivedFrom":sQuery(id+"F0.wireOp",EDGE,"E1.0")}),-1.0]])]});
            extrude(context, id + "F5", {"entities" : qUnion([Q0]), "operationType" : NewBodyOperationType.ADD, "depth" : 44.45 * mm});
        }
        {
            var Q0;
            Q0=makeQuery(id+"F0.imprint","IMPRINT",FACE,{"disambiguationData":[TD([[makeQuery(id+"F0.imprint","IMPRINT",EDGE,{"derivedFrom":sQuery(id+"F0.wireOp",EDGE,"E0.0")}),-1.0]])]});
            extrude(context, id + "F6", {"entities" : qUnion([Q0]), "operationType" : NewBodyOperationType.ADD, "depth" : 47.62 * mm});
        }
        {
            var Q0;
            Q0=qCreatedBy(makeId("Right.planeOp"),FACE);
            var sketch = newSketch(context, id + "F7", { "sketchPlane" : qUnion([Q0])});
            skLineSegment(sketch, "E16", {"start": v(0, 0) * mm, "end": v(0, 12.05) * mm});
            skLineSegment(sketch, "E17", {"start": v(0, 12.05) * mm, "end": v(12.05, 12.05) * mm});
            skLineSegment(sketch, "E18", {"start": v(12.05, 12.05) * mm, "end": v(12.05, 24.1) * mm});
            skLineSegment(sketch, "E19", {"start": v(12.05, 24.1) * mm, "end": v(24.1, 24.1) * mm});
            skLineSegment(sketch, "E20", {"start": v(24.1, 24.1) * mm, "end": v(24.1, 36.16) * mm});
            skLineSegment(sketch, "E21", {"start": v(24.1, 36.16) * mm, "end": v(36.16, 36.16) * mm});
            skLineSegment(sketch, "E22", {"start": v(36.16, 36.16) * mm, "end": v(36.16, 48.21) * mm});
            skLineSegment(sketch, "E23", {"start": v(36.16, 48.21) * mm, "end": v(48.21, 48.21) * mm});
            skLineSegment(sketch, "E24", {"start": v(48.21, 48.21) * mm, "end": v(48.21, 0) * mm});
            skLineSegment(sketch, "E25", {"start": v(48.21, 0) * mm, "end": v(0, 0) * mm});
            skLineSegment(sketch, "E26", {"start": v(0, 0) * mm, "end": v(0, 62.36) * mm});
            skSolve(sketch);
        }
        {
            var Q0;
            {var subQ0=sQuery(id+"F7.wireOp",EDGE,"E17");Q0=makeQuery(id+"F7.imprint","IMPRINT",FACE,{"disambiguationData":[TD([[makeQuery(id+"F7.imprint","IMPRINT",EDGE,{"derivedFrom":subQ0}),-1.0]])]});}
            var Q1;
            Q1=sQuery(id+"F7.wireOp",EDGE,"E26");
            revolve(context, id + "F8", {"entities" : qUnion([Q0]), "axis" : qUnion([Q1]), "revolveType" : RevolveType.FULL});
        }
        {
            var Q0;
            Q0=makeQuery(id+"F8.opRevolve","SWEPT_FACE",FACE,{"disambiguationData":[OSD([sQuery(id+"F7.wireOp",EDGE,"E17")])]});
            extrude(context, id + "F9", {"entities" : qUnion([Q0]), "operationType" : NewBodyOperationType.ADD, "depth" : 82.86 * mm});
        }
        {
            var Q0;
            Q0=qCreatedBy(makeId("Top.planeOp"),FACE);
            var sketch = newSketch(context, id + "F10", { "sketchPlane" : qUnion([Q0])});
            skCircle(sketch, "E27.cCircle", {"center": v(0, 0) * mm, "radius": 114.53 * mm, "construction": true});
            skLineSegment(sketch, "E27.0", {"start": v(-112.2, 33.45) * mm, "end": v(-88.9, 76.2) * mm});
            skLineSegment(sketch, "E27.1", {"start": v(-88.9, 76.2) * mm, "end": v(-50.22, 105.77) * mm});
            skLineSegment(sketch, "E27.2", {"start": v(-50.22, 105.77) * mm, "end": v(-2.86, 117.05) * mm});
            skLineSegment(sketch, "E27.3", {"start": v(-2.86, 117.05) * mm, "end": v(45, 108.1) * mm});
            skLineSegment(sketch, "E27.4", {"start": v(45, 108.1) * mm, "end": v(85.07, 80.45) * mm});
            skLineSegment(sketch, "E27.5", {"start": v(85.07, 80.45) * mm, "end": v(110.44, 38.89) * mm});
            skLineSegment(sketch, "E27.6", {"start": v(110.44, 38.89) * mm, "end": v(116.7, -9.4) * mm});
            skLineSegment(sketch, "E27.7", {"start": v(116.7, -9.4) * mm, "end": v(102.8, -56.05) * mm});
            skLineSegment(sketch, "E27.8", {"start": v(102.8, -56.05) * mm, "end": v(71.11, -93.02) * mm});
            skLineSegment(sketch, "E27.9", {"start": v(71.11, -93.02) * mm, "end": v(27.13, -113.9) * mm});
            skLineSegment(sketch, "E27.10", {"start": v(27.13, -113.9) * mm, "end": v(-21.54, -115.09) * mm});
            skLineSegment(sketch, "E27.11", {"start": v(-21.54, -115.09) * mm, "end": v(-66.49, -96.38) * mm});
            skLineSegment(sketch, "E27.12", {"start": v(-66.49, -96.38) * mm, "end": v(-99.94, -61) * mm});
            skLineSegment(sketch, "E27.13", {"start": v(-99.94, -61) * mm, "end": v(-116.11, -15.08) * mm});
            skLineSegment(sketch, "E27.14", {"start": v(-116.11, -15.08) * mm, "end": v(-112.2, 33.45) * mm});
            skPoint(sketch, "E27.0.midPoint", {"position": v(-100.55, 54.83) * mm});
            skSolve(sketch);
        }
        {
            var Q0;
            Q0=makeQuery(id+"F10.imprint","IMPRINT",FACE,{"disambiguationData":[TD([[makeQuery(id+"F10.imprint","IMPRINT",EDGE,{"derivedFrom":sQuery(id+"F10.wireOp",EDGE,"E27.0")}),-1.0]])]});
            extrude(context, id + "F11", {"entities" : qUnion([Q0]), "depth" : 12.7 * mm});
        }
        {
            var Q0;
            Q0=makeQuery(id+"F11.opExtrude","SWEPT_BODY",BODY,{"disambiguationData":[OSD([sQuery(id+"F10.wireOp",EDGE,"E27.0"),sQuery(id+"F10.wireOp",EDGE,"E27.1"),sQuery(id+"F10.wireOp",EDGE,"E27.2"),sQuery(id+"F10.wireOp",EDGE,"E27.3"),sQuery(id+"F10.wireOp",EDGE,"E27.4"),sQuery(id+"F10.wireOp",EDGE,"E27.5"),sQuery(id+"F10.wireOp",EDGE,"E27.6"),sQuery(id+"F10.wireOp",EDGE,"E27.7"),sQuery(id+"F10.wireOp",EDGE,"E27.8"),sQuery(id+"F10.wireOp",EDGE,"E27.9"),sQuery(id+"F10.wireOp",EDGE,"E27.10"),sQuery(id+"F10.wireOp",EDGE,"E27.11"),sQuery(id+"F10.wireOp",EDGE,"E27.12"),sQuery(id+"F10.wireOp",EDGE,"E27.13"),sQuery(id+"F10.wireOp",EDGE,"E27.14")])]});
            transform(context, id + "F12", {"entities" : qUnion([Q0]), "transformType" : TransformType.TRANSLATION_3D, "dx" : 0 * mm, "dy" : 0 * mm, "dz" : 94.94 * mm, "makeCopy" : false});
        }
    });
